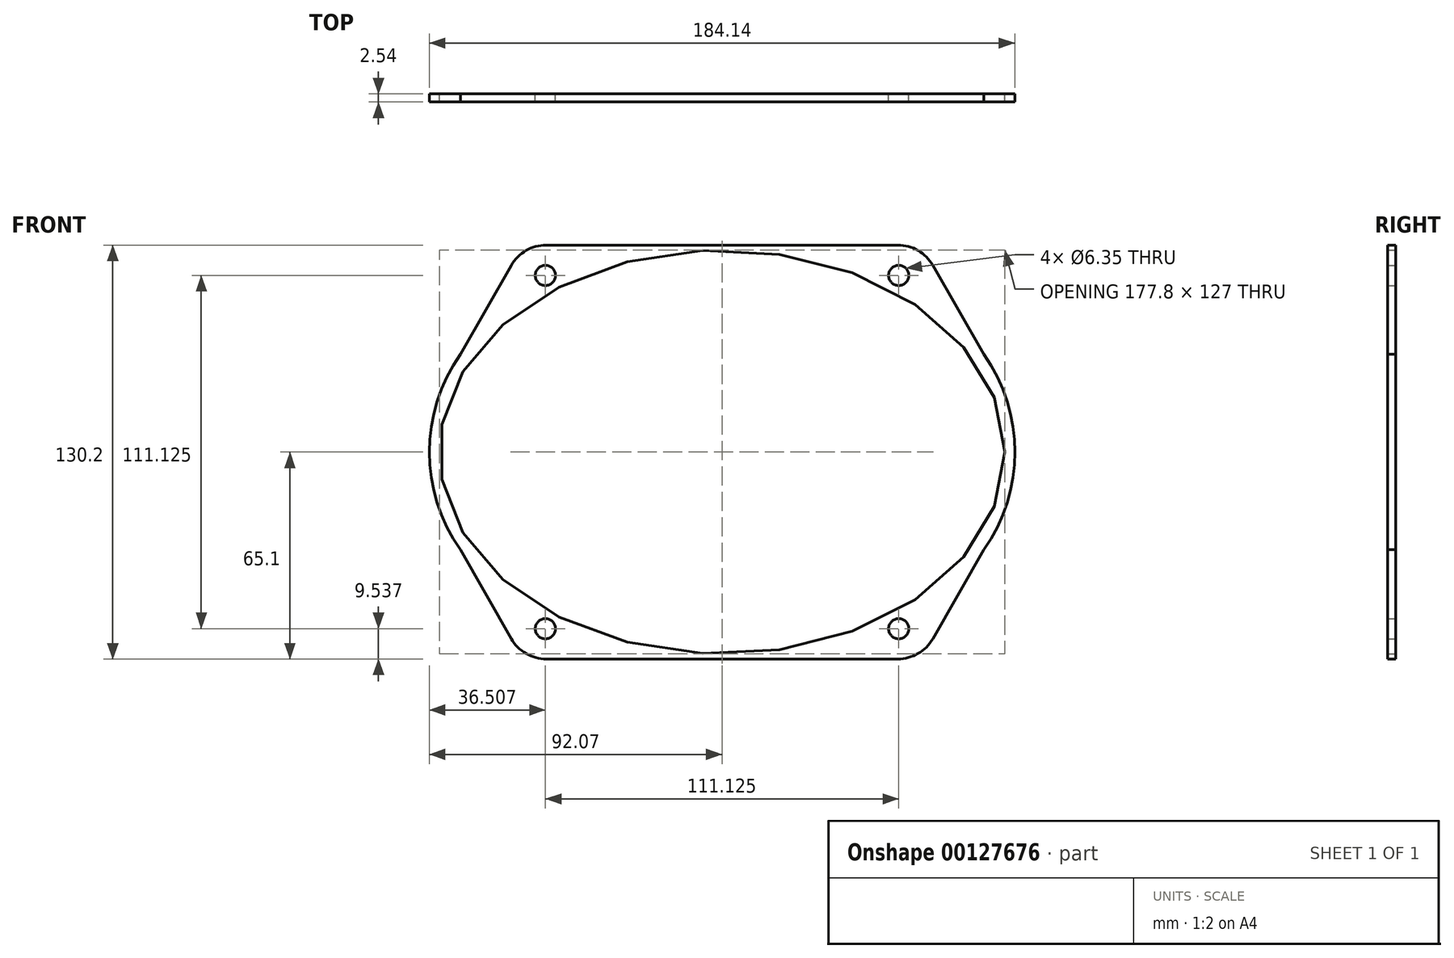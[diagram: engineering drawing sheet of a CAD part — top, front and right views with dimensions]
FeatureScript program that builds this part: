
annotation { "Feature Type Name" : "Feature", "Feature Type Description" : "" }
export const myFeature = defineFeature(function(context is Context, id is Id, definition is map)
    precondition{}
    {
        {
            var Q0;
            Q0=qCreatedBy(makeId("Front.planeOp"),FACE);
            var sketch = newSketch(context, id + "F0", { "sketchPlane" : qUnion([Q0])});
            skCircle(sketch, "E0", {"center": v(-55.56, 55.56) * mm, "radius": 3.18 * mm});
            skCircle(sketch, "E1.MirrorC", {"center": v(55.56, 55.56) * mm, "radius": 3.18 * mm});
            skCircle(sketch, "E2.MirrorC", {"center": v(55.56, -55.56) * mm, "radius": 3.18 * mm});
            skCircle(sketch, "E3.MirrorC", {"center": v(-55.56, -55.56) * mm, "radius": 3.18 * mm});
            skEllipse(sketch, "E4", {"center": v(0, 0) * mm, "majorRadius": 88.9 * mm, "minorRadius": 63.5 * mm, "majorAxis": v(1, 0)});
            skLineSegment(sketch, "E5", {"start": v(-92.08, 65.1) * mm, "end": v(-55.28, 65.1) * mm, "construction": true});
            skPoint(sketch, "E5.endSnap0", {"position": v(0, 63.5) * mm});
            skLineSegment(sketch, "E6", {"start": v(-92.08, 65.1) * mm, "end": v(-92.08, 0) * mm, "construction": true});
            skArc(sketch, "E7", {"start": v(-82.3, 30.74) * mm, "mid": v(-89.57, 16.13) * mm, "end": v(-92.08, 0) * mm});
            skLineSegment(sketch, "E8", {"start": v(-82.3, 30.74) * mm, "end": v(-66.3, 58.7) * mm});
            skLineSegment(sketch, "E9", {"start": v(-55.28, 65.1) * mm, "end": v(0, 65.1) * mm});
            skPoint(sketch, "E10.visualSharp", {"position": v(-62.64, 65.1) * mm});
            skArc(sketch, "E10.filletArc", {"start": v(-55.28, 65.1) * mm, "mid": v(-61.65, 63.39) * mm, "end": v(-66.3, 58.7) * mm});
            skLineSegment(sketch, "E11.MirrorCS", {"start": v(82.3, 30.74) * mm, "end": v(66.3, 58.7) * mm});
            skLineSegment(sketch, "E12.MirrorCS", {"start": v(55.28, 65.1) * mm, "end": v(0, 65.1) * mm});
            skArc(sketch, "E13.MirrorCS", {"start": v(55.28, 65.1) * mm, "mid": v(61.65, 63.39) * mm, "end": v(66.3, 58.7) * mm});
            skArc(sketch, "E14.MirrorCS", {"start": v(82.3, 30.74) * mm, "mid": v(89.57, 16.13) * mm, "end": v(92.08, 0) * mm});
            skArc(sketch, "E15.MirrorCS", {"start": v(82.3, -30.74) * mm, "mid": v(89.57, -16.13) * mm, "end": v(92.08, 0) * mm});
            skLineSegment(sketch, "E16.MirrorCS", {"start": v(82.3, -30.74) * mm, "end": v(66.3, -58.7) * mm});
            skArc(sketch, "E17.MirrorCS", {"start": v(55.28, -65.1) * mm, "mid": v(61.65, -63.39) * mm, "end": v(66.3, -58.7) * mm});
            skLineSegment(sketch, "E18.MirrorCS", {"start": v(55.28, -65.1) * mm, "end": v(0, -65.1) * mm});
            skLineSegment(sketch, "E19.MirrorCS", {"start": v(-82.3, -30.74) * mm, "end": v(-66.3, -58.7) * mm});
            skLineSegment(sketch, "E20.MirrorCS", {"start": v(-55.28, -65.1) * mm, "end": v(0, -65.1) * mm});
            skArc(sketch, "E21.MirrorCS", {"start": v(-55.28, -65.1) * mm, "mid": v(-61.65, -63.39) * mm, "end": v(-66.3, -58.7) * mm});
            skArc(sketch, "E22.MirrorCS", {"start": v(-82.3, -30.74) * mm, "mid": v(-89.57, -16.13) * mm, "end": v(-92.08, 0) * mm});
            skSolve(sketch);
        }
        {
            var Q0;
            Q0=makeQuery(id+"F0.imprint","IMPRINT",FACE,{"disambiguationData":[TD([[makeQuery(id+"F0.imprint","IMPRINT",EDGE,{"derivedFrom":sQuery(id+"F0.wireOp",EDGE,"E0")}),-1.0]])]});
            extrude(context, id + "F1", {"entities" : qUnion([Q0]), "depth" : 2.54 * mm});
        }
    });
